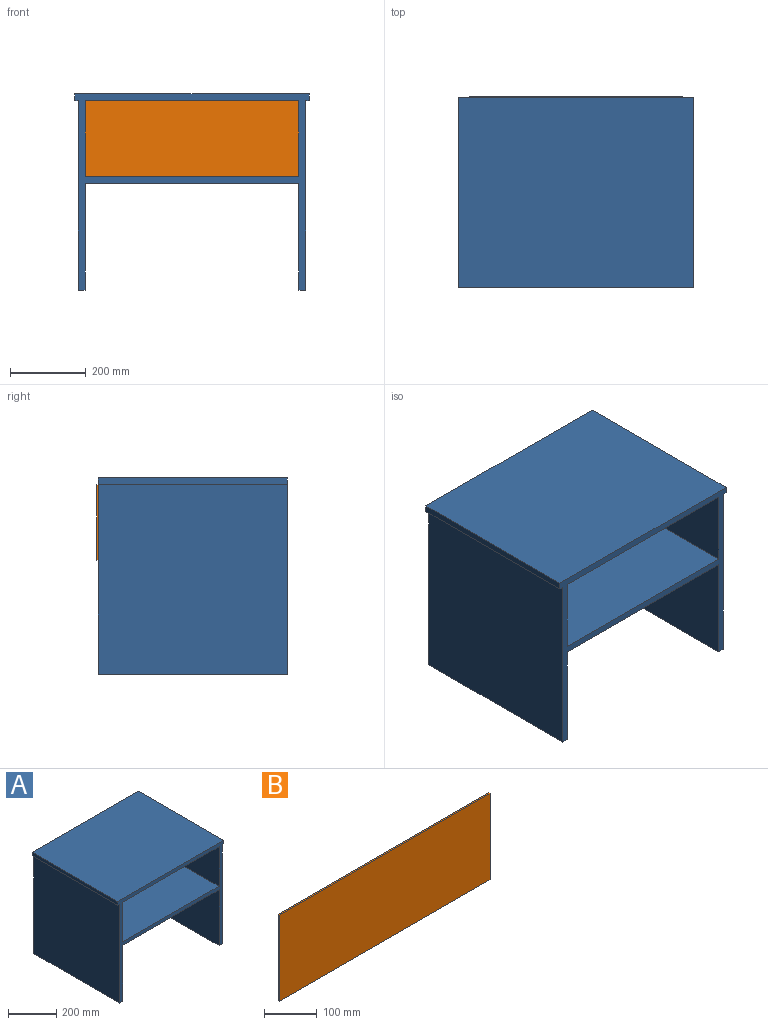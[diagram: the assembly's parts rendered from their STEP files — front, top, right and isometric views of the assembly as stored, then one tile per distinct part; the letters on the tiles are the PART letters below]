
ASSEMBLY  parts=2 mates=1
PART A: 18 faces, bbox 620x500x518 mm
  f0: plane 500x282mm, normal (1,0,0), area 141000mm2, adj f1,f15,f16,f17
  f1: plane 564x500mm, normal (0,0,-1), area 282000mm2, adj f0,f2,f16,f17
  f2: plane 500x282mm, normal (-1,0,0), area 141000mm2, adj f1,f3,f16,f17
  f3: plane 500x18mm, normal (0,0,-1), area 9000mm2, adj f2,f4,f16,f17
  f4: plane 500x500mm, normal (1,0,0), area 250000mm2, adj f3,f5,f16,f17
  f5: plane 500x10mm, normal (0,0,-1), area 5000mm2, adj f4,f6,f16,f17
  f6: plane 500x18mm, normal (1,0,0), area 9000mm2, adj f5,f7,f16,f17
  f7: plane 620x500mm, normal (0,0,1), area 310000mm2, adj f6,f8,f16,f17
  f8: plane 500x18mm, normal (-1,0,0), area 9000mm2, adj f7,f9,f16,f17
  f9: plane 500x10mm, normal (0,0,-1), area 5000mm2, adj f8,f10,f16,f17
  f10: plane 500x500mm, normal (-1,0,0), area 250000mm2, adj f9,f15,f16,f17
  f11: plane 564x500mm, normal (0,0,1), area 282000mm2, adj f12,f14,f16,f17
  f12: plane 500x200mm, normal (1,0,0), area 100000mm2, adj f11,f13,f16,f17
  f13: plane 564x500mm, normal (0,0,-1), area 282000mm2, adj f12,f14,f16,f17
  f14: plane 500x200mm, normal (-1,0,0), area 100000mm2, adj f11,f13,f16,f17
  f15: plane 500x18mm, normal (0,0,-1), area 9000mm2, adj f0,f10,f16,f17
  f16: plane 620x518mm, normal (0,-1,0), area 39312mm2, adj f0,f1,f2,f3,f4,f5,f6,f7
  f17: plane 620x518mm, normal (0,1,0), area 39312mm2, adj f0,f1,f2,f3,f4,f5,f6,f7
PART B: 6 faces, bbox 564x4x200 mm
  f0: plane 200x4mm, normal (-1,0,0), area 800mm2, adj f1,f3,f4,f5
  f1: plane 564x4mm, normal (0,0,-1), area 2256mm2, adj f0,f2,f4,f5
  f2: plane 200x4mm, normal (1,0,0), area 800mm2, adj f1,f3,f4,f5
  f3: plane 564x4mm, normal (0,0,1), area 2256mm2, adj f0,f2,f4,f5
  f4: plane 564x200mm, normal (0,-1,0), area 112800mm2, adj f0,f1,f2,f3
  f5: plane 564x200mm, normal (0,1,0), area 112800mm2, adj f0,f1,f2,f3
PLACE A t=(-131.12,136.09,-106.95)mm
PLACE B t=(-113.12,140.09,193.05)mm
MATE fastened B.f4 <-> A.f17  axis (0,-1,0) through (450.88,136.09,393.05)mm
